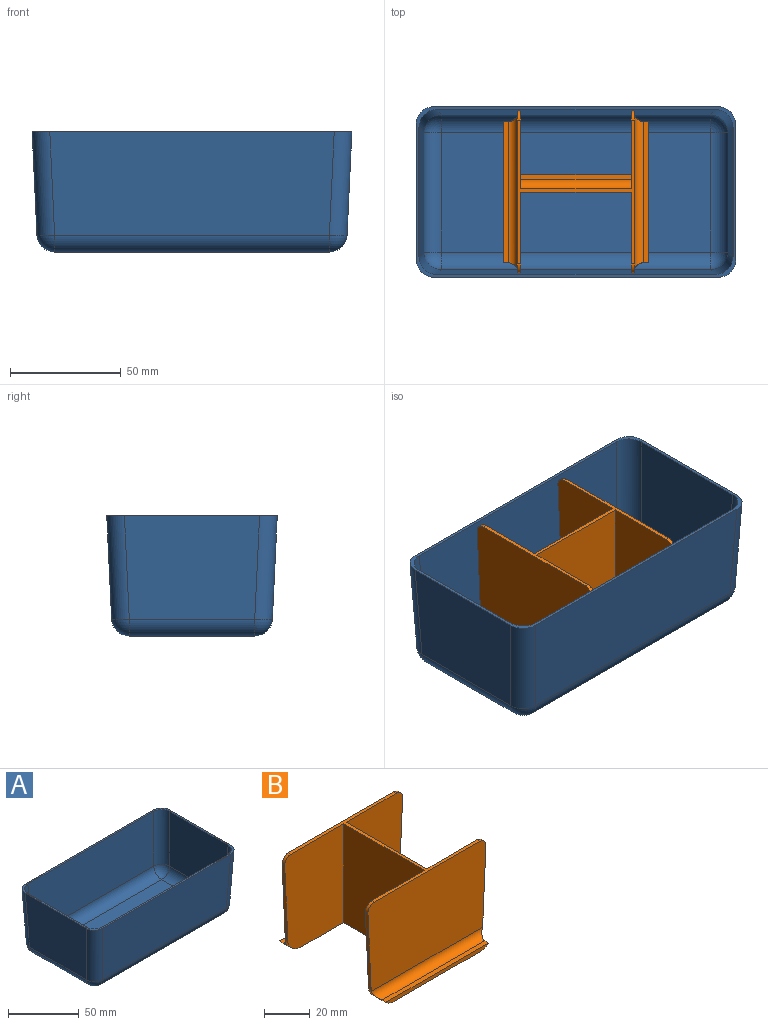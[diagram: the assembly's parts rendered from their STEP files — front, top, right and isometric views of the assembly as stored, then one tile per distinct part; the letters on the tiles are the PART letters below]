
ASSEMBLY  parts=2 mates=1
PART A: 35 faces, bbox 144.6x77.1x54.5 mm
  f0: plane 61.12x46.68mm, normal (1,0,-0.05), area 2753.1mm2, adj f8,f13,f16,f26
  f1: plane 128.62x46.68mm, normal (0,1,-0.05), area 5907.3mm2, adj f8,f13,f14,f22
  f2: plane 61.12x46.68mm, normal (-1,0,-0.05), area 2753.1mm2, adj f8,f14,f15,f19
  f3: plane 58.52x45.38mm, normal (1,0,0.05), area 2561.1mm2, adj f8,f9,f12,f32
  f4: plane 126.02x45.38mm, normal (0,-1,0.05), area 5627.4mm2, adj f8,f9,f10,f28
  f5: plane 58.52x45.38mm, normal (-1,0,0.05), area 2561.1mm2, adj f8,f10,f11,f29
  f6: plane 126.02x45.38mm, normal (0,1,0.05), area 5627.4mm2, adj f8,f11,f12,f33
  f7: plane 128.62x46.68mm, normal (0,-1,-0.05), area 5907.3mm2, adj f8,f15,f16,f23
  f8: plane 144.6x77.1mm, normal (0,0,1), area 569.7mm2, adj f0,f1,f2,f3,f4,f5,f6,f7
  f9: cylinder r=8mm len=45.69mm, axis (0.05,-0.05,-1), area 572mm2, adj f3,f4,f8,f30
  f10: cylinder r=8mm len=45.69mm, axis (-0.05,-0.05,-1), area 572mm2, adj f4,f5,f8,f27
  f11: cylinder r=8mm len=45.69mm, axis (-0.05,0.05,-1), area 572mm2, adj f5,f6,f8,f31
  f12: cylinder r=8mm len=45.69mm, axis (0.05,0.05,-1), area 572mm2, adj f3,f6,f8,f34
  f13: cylinder r=8mm len=46.99mm, axis (0.05,0.05,1), area 588.3mm2, adj f0,f1,f8,f24
  f14: cylinder r=8mm len=46.99mm, axis (-0.05,0.05,1), area 588.3mm2, adj f1,f2,f8,f20
  f15: cylinder r=8mm len=46.99mm, axis (-0.05,-0.05,1), area 588.3mm2, adj f2,f7,f8,f21
  f16: cylinder r=8mm len=46.99mm, axis (0.05,-0.05,1), area 588.3mm2, adj f0,f7,f8,f25
  f17: plane 121.74x54.24mm, normal (0,0,1), area 6602.8mm2, adj f28,f29,f32,f33
  f18: plane 124.22x56.72mm, normal (0,0,-1), area 7044.9mm2, adj f19,f22,f23,f26
  f19: cylinder r=8mm len=56.72mm, axis (0,1,0), area 691.3mm2, adj f2,f18,f20,f21
  f20: sphere r=8mm, area 94.5mm2, adj f14,f19,f22
  f21: sphere r=8mm, area 94.5mm2, adj f15,f19,f23
  f22: cylinder r=8mm len=124.22mm, axis (1,0,0), area 1514.1mm2, adj f1,f18,f20,f24
  f23: cylinder r=8mm len=124.22mm, axis (1,0,0), area 1514.1mm2, adj f7,f18,f21,f25
  f24: sphere r=8mm, area 94.5mm2, adj f13,f22,f26
  f25: sphere r=8mm, area 94.5mm2, adj f16,f23,f26
  f26: cylinder r=8mm len=56.72mm, axis (0,-1,0), area 691.3mm2, adj f0,f18,f24,f25
  f27: sphere r=8mm, area 94.5mm2, adj f10,f28,f29
  f28: cylinder r=8mm len=121.74mm, axis (-1,0,0), area 1483.9mm2, adj f4,f17,f27,f30
  f29: cylinder r=8mm len=54.24mm, axis (0,-1,0), area 661.1mm2, adj f5,f17,f27,f31
  f30: sphere r=8mm, area 94.5mm2, adj f9,f28,f32
  f31: sphere r=8mm, area 94.5mm2, adj f11,f29,f33
  f32: cylinder r=8mm len=54.24mm, axis (0,-1,0), area 661.1mm2, adj f3,f17,f30,f34
  f33: cylinder r=8mm len=121.74mm, axis (-1,0,0), area 1483.9mm2, adj f6,f17,f31,f34
  f34: sphere r=8mm, area 94.5mm2, adj f12,f32,f33
PART B: 31 faces, bbox 73.1x66x53 mm
  f0: plane 66x53.24mm, normal (0,0,-1), area 1251.8mm2, adj f1,f5,f6,f7,f10,f13,f14,f17
  f1: plane 50x2mm, normal (1,0,0), area 100mm2, adj f0,f2,f10,f13
  f2: plane 50x2.4mm, normal (0,0,1), area 120mm2, adj f1,f10,f13,f26
  f3: plane 50x47mm, normal (1,0,0), area 2350mm2, adj f4,f10,f13,f26
  f4: plane 65.11x53.2mm, normal (0,0,1), area 288.4mm2, adj f3,f5,f6,f9,f10,f13,f14,f15
  f5: plane 53x50mm, normal (-1,0,0), area 2650mm2, adj f0,f4,f6,f14
  f6: plane 53x36.56mm, normal (0,-1,0), area 1865.4mm2, adj f0,f4,f5,f12,f22,f29
  f7: plane 63.82x2mm, normal (0,1,0), area 121mm2, adj f0,f8,f22,f23
  f8: plane 63.82x2.4mm, normal (0,0,1), area 153.2mm2, adj f7,f22,f23,f24
  f9: plane 73.11x47mm, normal (0,1,0), area 3342.5mm2, adj f4,f11,f12,f22,f23,f24,f29,f30
  f10: plane 53x34.96mm, normal (0,-1,0), area 1764.4mm2, adj f0,f1,f2,f3,f4,f11,f23,f26
  f11: plane 41.19x1.94mm, normal (1,0,-0.05), area 66mm2, adj f9,f10,f23,f30
  f12: plane 41.19x1.94mm, normal (-1,0,-0.05), area 66mm2, adj f6,f9,f22,f29
  f13: plane 53x34.96mm, normal (0,1,0), area 1764.4mm2, adj f0,f1,f2,f3,f4,f18,f21,f26
  f14: plane 53x36.56mm, normal (0,1,0), area 1865.4mm2, adj f0,f4,f5,f19,f20,f27
  f15: plane 73.11x47mm, normal (0,-1,0), area 3342.5mm2, adj f4,f18,f19,f20,f21,f25,f27,f28
  f16: plane 63.82x2.4mm, normal (0,0,1), area 153.2mm2, adj f17,f20,f21,f25
  f17: plane 63.82x2mm, normal (0,-1,0), area 121mm2, adj f0,f16,f20,f21
  f18: plane 41.19x1.94mm, normal (1,0,-0.05), area 66mm2, adj f13,f15,f21,f28
  f19: plane 41.19x1.94mm, normal (-1,0,-0.05), area 66mm2, adj f14,f15,f20,f27
  f20: cylinder r=8mm len=8mm, axis (0,1,0), area 61.1mm2, adj f0,f14,f15,f16,f17,f19,f25
  f21: cylinder r=8mm len=8mm, axis (0,1,0), area 61.1mm2, adj f0,f13,f15,f16,f17,f18,f25
  f22: cylinder r=8mm len=8mm, axis (0,1,0), area 61.1mm2, adj f0,f6,f7,f8,f9,f12,f24
  f23: cylinder r=8mm len=8mm, axis (0,1,0), area 61.1mm2, adj f0,f7,f8,f9,f10,f11,f24
  f24: cylinder r=4mm len=68.73mm, axis (-1,0,0), area 415.1mm2, adj f8,f9,f22,f23
  f25: cylinder r=4mm len=68.73mm, axis (1,0,0), area 415.1mm2, adj f15,f16,f20,f21
  f26: cylinder r=4mm len=50mm, axis (0,1,0), area 314.2mm2, adj f2,f3,f10,f13
  f27: cylinder r=4mm len=4.19mm, axis (0,-1,0), area 10.4mm2, adj f4,f14,f15,f19
  f28: cylinder r=4mm len=4.19mm, axis (0,-1,0), area 10.4mm2, adj f4,f13,f15,f18
  f29: cylinder r=4mm len=4.19mm, axis (0,-1,0), area 10.4mm2, adj f4,f6,f9,f12
  f30: cylinder r=4mm len=4.19mm, axis (0,-1,0), area 10.4mm2, adj f4,f9,f10,f11
PLACE A t=(-46.38,-20.9,-6.43)mm
PLACE B rot(axis=(0,0,1),90deg) t=(-46.38,-20.9,-6.43)mm
MATE revolute B.f0 <-> A.f17  axis (0,0,1) through (-46.38,-20.9,-6.43)mm
